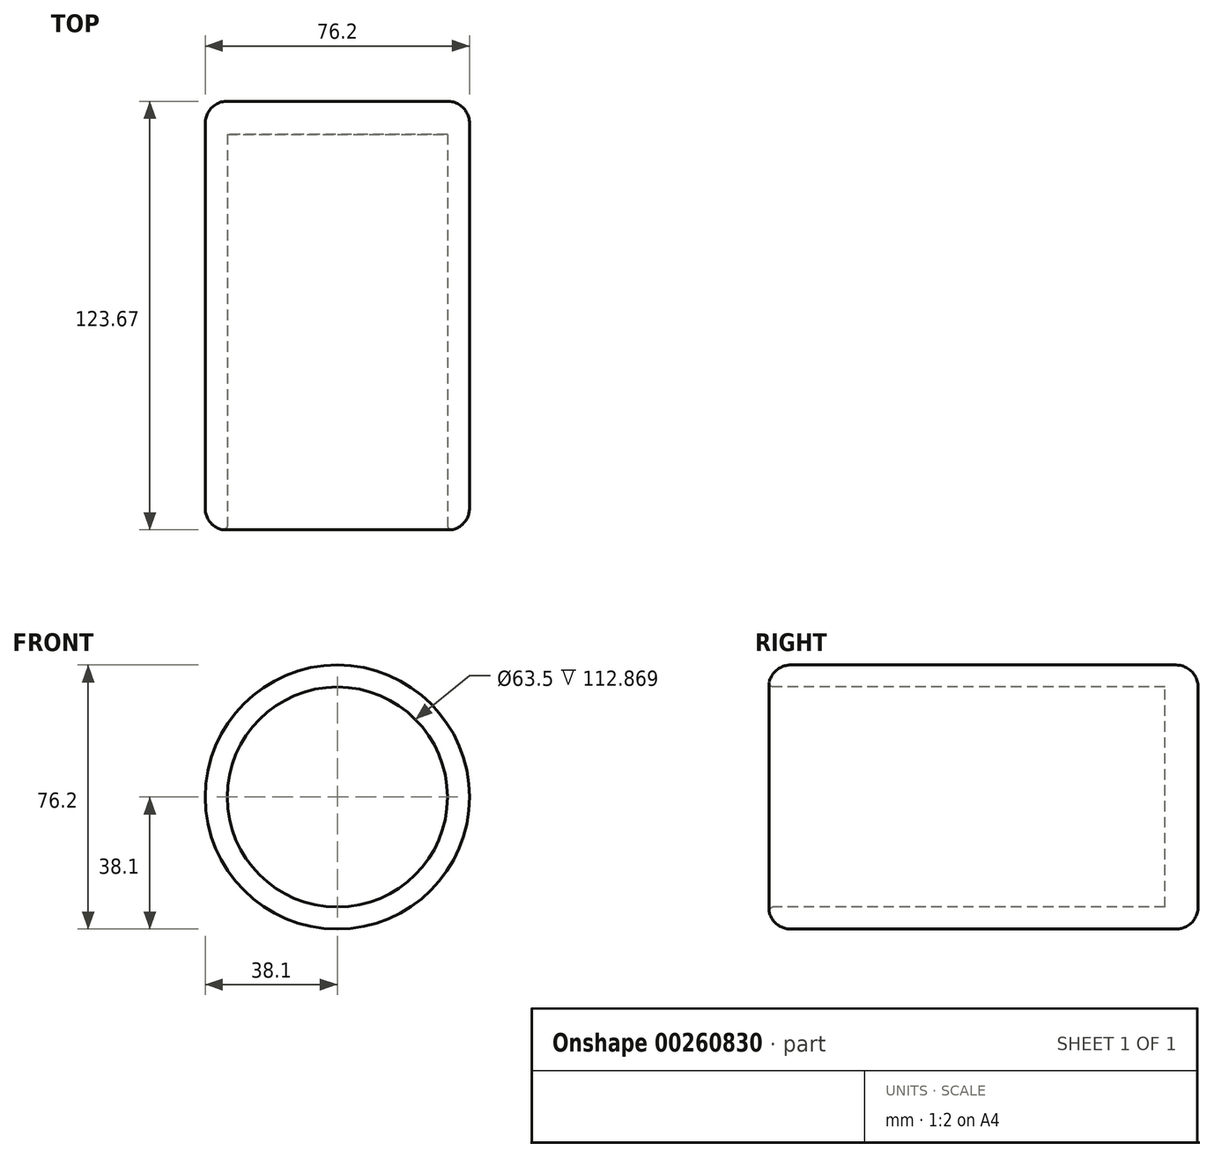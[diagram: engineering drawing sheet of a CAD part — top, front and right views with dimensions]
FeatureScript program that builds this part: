
annotation { "Feature Type Name" : "Feature", "Feature Type Description" : "" }
export const myFeature = defineFeature(function(context is Context, id is Id, definition is map)
    precondition{}
    {
        {
            var Q0;
            Q0=qCreatedBy(makeId("Front.planeOp"),FACE);
            var sketch = newSketch(context, id + "F0", { "sketchPlane" : qUnion([Q0])});
            skCircle(sketch, "E0", {"center": v(0, 0) * mm, "radius": 38.1 * mm});
            skSolve(sketch);
        }
        {
            var Q0;
            Q0 = qSketchRegion(id + "F0", true);
            extrude(context, id + "F1", {"entities" : qUnion([Q0]), "oppositeDirection" : true, "depth" : 123.82 * mm});
        }
        {
            var Q0;
            Q0=qCreatedBy(makeId("Front.planeOp"),FACE);
            var sketch = newSketch(context, id + "F2", { "sketchPlane" : qUnion([Q0])});
            skCircle(sketch, "E1", {"center": v(0, 0) * mm, "radius": 31.75 * mm});
            skSolve(sketch);
        }
        {
            var Q0;
            Q0=makeQuery(id+"F2.imprint","IMPRINT",FACE,{"disambiguationData":[TD([[makeQuery(id+"F2.imprint","IMPRINT",EDGE,{"derivedFrom":sQuery(id+"F2.wireOp",EDGE,"E1")}),1.0]])]});
            extrude(context, id + "F3", {"entities" : qUnion([Q0]), "operationType" : NewBodyOperationType.REMOVE, "oppositeDirection" : true, "depth" : 114.3 * mm});
        }
        {
            var Q0;
            Q0=makeQuery(id+"F1.opExtrude","CAP_EDGE",EDGE,{"disambiguationData":[OSD([sQuery(id+"F0.wireOp",EDGE,"E0")])],"isStart":true});
            fillet(context, id + "F4", {"entities" : qUnion([Q0]), "radius" : 6.35 * mm, "tangentPropagation" : true, "allowEdgeOverflow" : false});
        }
        {
            var Q0;
            Q0=makeQuery(id+"F1.opExtrude","CAP_EDGE",EDGE,{"disambiguationData":[OSD([sQuery(id+"F0.wireOp",EDGE,"E0")])],"isStart":false});
            fillet(context, id + "F5", {"entities" : qUnion([Q0]), "radius" : 6.35 * mm, "tangentPropagation" : true, "allowEdgeOverflow" : false});
        }
        {
            var Q0;
            Q0=makeQuery(id+"F4.opFillet","BLEND_EDGE",EDGE,{"blendedFrom":[makeQuery(id+"F1.opExtrude","CAP_EDGE",EDGE,{"disambiguationData":[OSD([sQuery(id+"F0.wireOp",EDGE,"E0")])],"isStart":true}),makeQuery(id+"F3.boolean.opBoolean","COPY",FACE,{"derivedFrom":makeQuery(id+"F3.opExtrude","SWEPT_FACE",FACE,{"disambiguationData":[OSD([sQuery(id+"F2.wireOp",EDGE,"E1")])]})})],"blendedInto":[makeQuery(id+"F3.boolean.opBoolean","COPY",FACE,{"derivedFrom":makeQuery(id+"F3.opExtrude","SWEPT_FACE",FACE,{"disambiguationData":[OSD([sQuery(id+"F2.wireOp",EDGE,"E1")])]})})]});
            fillet(context, id + "F6", {"entities" : qUnion([Q0]), "radius" : 1.27 * mm, "tangentPropagation" : true, "allowEdgeOverflow" : false});
        }
    });
